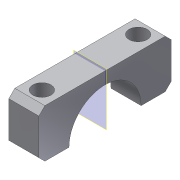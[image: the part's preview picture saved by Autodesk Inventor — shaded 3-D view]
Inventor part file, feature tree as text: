
AUTODESK INVENTOR PART (.ipt)
format: ipt  version: 2015 (Build 190159000, 159)  size: 109,568 bytes
history: native  units: mm
features: sketch x2, extrude x1, plane x1, hole x1, chamfer x1
ambient origin geometry x8: Origin, YZ Plane, XZ Plane, XY Plane, X Axis, Y Axis, Z Axis, Center Point
bodies: Volumenkörper1 (feature_tree)
feature tree (6):
  extrude  "Extrusion1"  Depth=5.0mm TaperAngle=0.0deg
  plane  "Arbeitsebene2"
  hole  "Bohrung2"  [1 undecoded]
  chamfer  "Fase1"  Distance=16.0mm
  sketch  "Skizze1"  dims[d2=6.0mm d4=5.0mm d5=0.0mm]
  sketch  "Skizze5"  dims[d18=22.0mm d26=8.0mm d27=16.0mm d28=2.5mm d29=3.0mm d30=6.0mm d31=4.0mm d32=2.0mm d33=90.0deg d34=8.0mm d35=20.594885mm d36=1.0mm d37=2.0mm d38=45.0deg]
note: 1 required parameter value undecoded (feature->parameter linkage not recoverable at this tier; creation-order binding heuristic only, values carry confidence <= 0.55)
